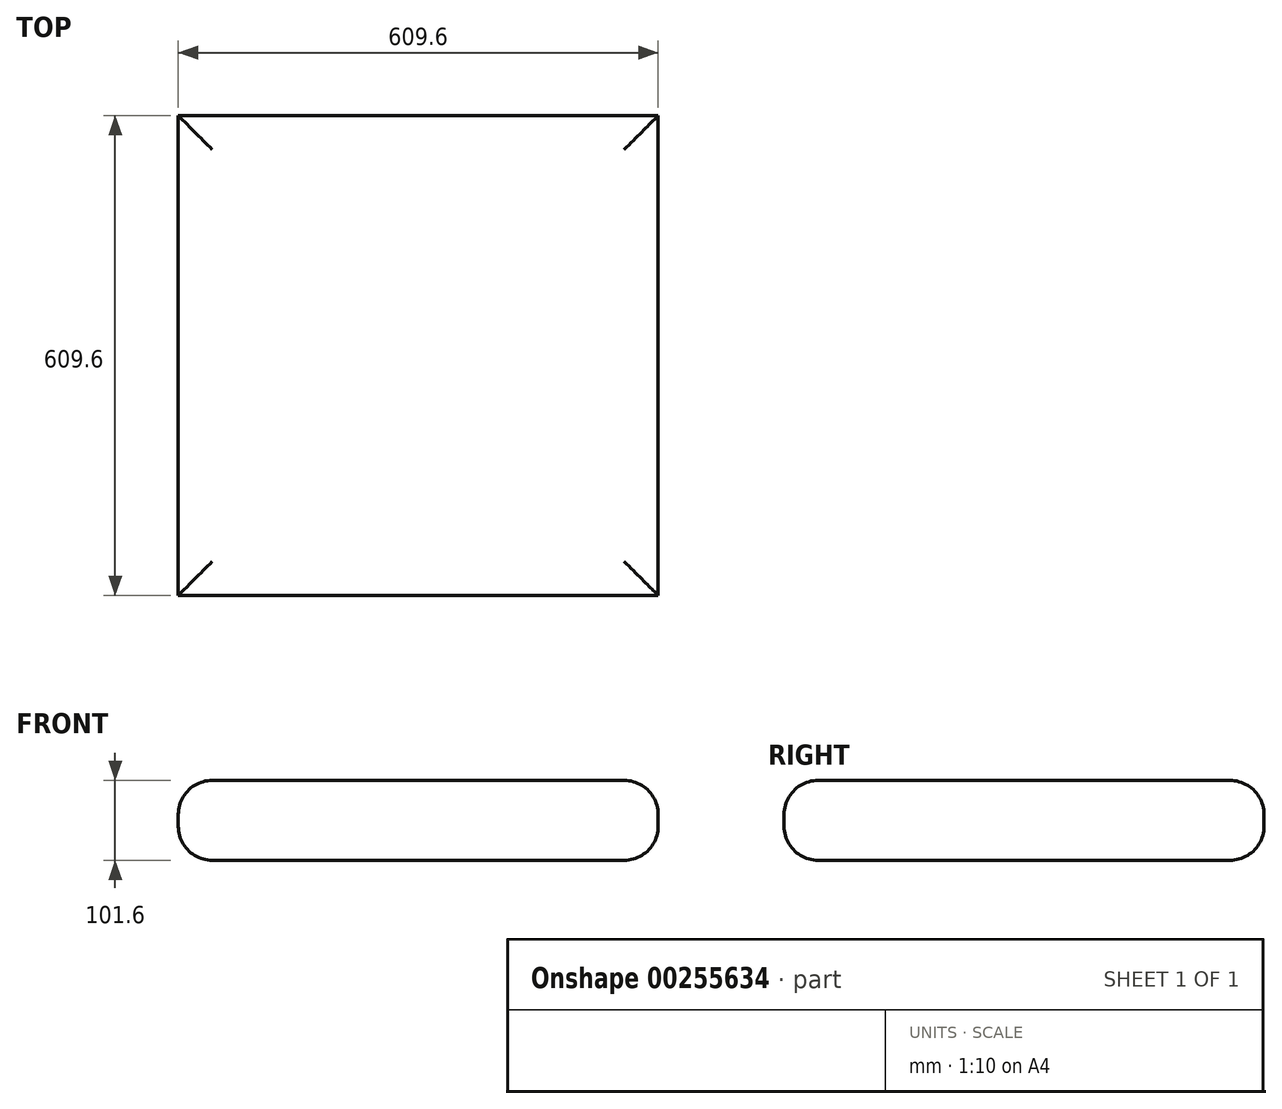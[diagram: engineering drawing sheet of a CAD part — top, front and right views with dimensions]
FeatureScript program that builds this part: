
annotation { "Feature Type Name" : "Feature", "Feature Type Description" : "" }
export const myFeature = defineFeature(function(context is Context, id is Id, definition is map)
    precondition{}
    {
        {
            var Q0;
            Q0=qCreatedBy(makeId("Top.planeOp"),FACE);
            var sketch = newSketch(context, id + "F0", { "sketchPlane" : qUnion([Q0])});
            skLineSegment(sketch, "E0.bottom", {"start": v(-601.94, 634.75) * mm, "end": v(7.66, 634.75) * mm});
            skLineSegment(sketch, "E0.top", {"start": v(-601.94, 25.15) * mm, "end": v(7.66, 25.15) * mm});
            skLineSegment(sketch, "E0.left", {"start": v(-601.94, 634.75) * mm, "end": v(-601.94, 25.15) * mm});
            skLineSegment(sketch, "E0.right", {"start": v(7.66, 634.75) * mm, "end": v(7.66, 25.15) * mm});
            skSolve(sketch);
        }
        {
            var Q0;
            Q0 = qSketchRegion(id + "F0", true);
            extrude(context, id + "F1", {"entities" : qUnion([Q0]), "depth" : 101.6 * mm});
        }
        {
            var Q0;
            Q0=makeQuery(id+"F1.opExtrude","CAP_FACE",FACE,{"disambiguationData":[OSD([sQuery(id+"F0.wireOp",EDGE,"E0.bottom"),sQuery(id+"F0.wireOp",EDGE,"E0.top"),sQuery(id+"F0.wireOp",EDGE,"E0.left"),sQuery(id+"F0.wireOp",EDGE,"E0.right")])],"isStart":false});
            var Q1;
            Q1=makeQuery(id+"F1.opExtrude","CAP_FACE",FACE,{"disambiguationData":[OSD([sQuery(id+"F0.wireOp",EDGE,"E0.bottom"),sQuery(id+"F0.wireOp",EDGE,"E0.top"),sQuery(id+"F0.wireOp",EDGE,"E0.left"),sQuery(id+"F0.wireOp",EDGE,"E0.right")])],"isStart":true});
            fillet(context, id + "F2", {"entities" : qUnion([Q0, Q1]), "radius" : 43.18 * mm, "tangentPropagation" : true, "allowEdgeOverflow" : false});
        }
    });
